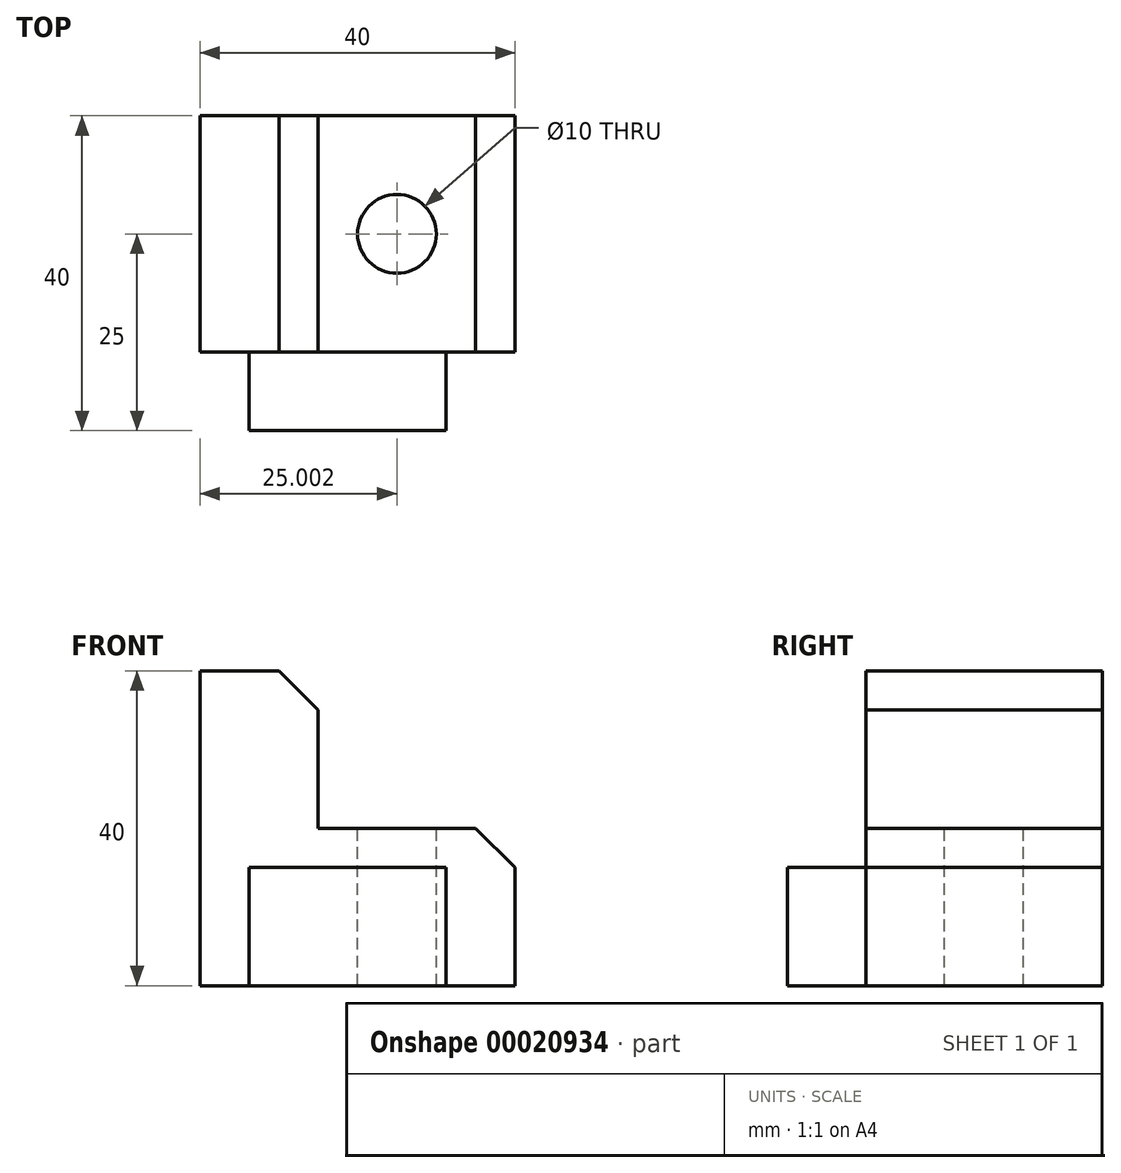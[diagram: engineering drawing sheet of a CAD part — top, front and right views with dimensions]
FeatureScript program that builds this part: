
annotation { "Feature Type Name" : "Feature", "Feature Type Description" : "" }
export const myFeature = defineFeature(function(context is Context, id is Id, definition is map)
    precondition{}
    {
        {
            var Q0;
            Q0=qCreatedBy(makeId("Front.planeOp"),FACE);
            var sketch = newSketch(context, id + "F0", { "sketchPlane" : qUnion([Q0])});
            skLineSegment(sketch, "E0", {"start": v(-37.6, 38.9) * mm, "end": v(-37.6, -1.1) * mm});
            skLineSegment(sketch, "E1", {"start": v(-37.6, -1.1) * mm, "end": v(2.4, -1.1) * mm});
            skLineSegment(sketch, "E2", {"start": v(2.4, -1.1) * mm, "end": v(2.4, 18.9) * mm});
            skLineSegment(sketch, "E3", {"start": v(2.4, 18.9) * mm, "end": v(-22.6, 18.9) * mm});
            skLineSegment(sketch, "E4", {"start": v(-22.6, 18.9) * mm, "end": v(-22.6, 38.9) * mm});
            skLineSegment(sketch, "E5", {"start": v(-22.6, 38.9) * mm, "end": v(-37.6, 38.9) * mm});
            skSolve(sketch);
        }
        {
            var Q0;
            Q0=makeQuery(id+"F0.imprint","IMPRINT",FACE,{"disambiguationData":[TD([[makeQuery(id+"F0.imprint","IMPRINT",EDGE,{"derivedFrom":sQuery(id+"F0.wireOp",EDGE,"E0")}),1.0]])]});
            extrude(context, id + "F1", {"entities" : qUnion([Q0]), "depth" : 30 * mm});
        }
        {
            var Q0;
            Q0=makeQuery(id+"F1.opExtrude","SWEPT_EDGE",EDGE,{"disambiguationData":[OSD([sQuery(id+"F0.wireOp",EDGE,"E4"),sQuery(id+"F0.wireOp",EDGE,"E5")])]});
            var Q1;
            Q1=makeQuery(id+"F1.opExtrude","SWEPT_EDGE",EDGE,{"disambiguationData":[OSD([sQuery(id+"F0.wireOp",EDGE,"E2"),sQuery(id+"F0.wireOp",EDGE,"E3")])]});
            chamfer(context, id + "F2", {"entities" : qUnion([Q0, Q1]), "width" : 5 * mm, "tangentPropagation" : true});
        }
        {
            var Q0;
            Q0=makeQuery(id+"F1.opExtrude","SWEPT_FACE",FACE,{"disambiguationData":[OSD([sQuery(id+"F0.wireOp",EDGE,"E3")])]});
            var sketch = newSketch(context, id + "F3", { "sketchPlane" : qUnion([Q0])});
            skCircle(sketch, "E6", {"center": v(-12.6, -15) * mm, "radius": 5 * mm});
            skSolve(sketch);
        }
        {
            var Q0;
            Q0=makeQuery(id+"F3.imprint","IMPRINT",FACE,{"disambiguationData":[TD([[makeQuery(id+"F3.imprint","IMPRINT",EDGE,{"derivedFrom":sQuery(id+"F3.wireOp",EDGE,"E6")}),1.0]])]});
            extrude(context, id + "F4", {"entities" : qUnion([Q0]), "operationType" : NewBodyOperationType.REMOVE, "endBound" : BoundingType.THROUGH_ALL, "oppositeDirection" : true, "depth" : 25 * mm});
        }
        {
            var Q0;
            Q0=makeQuery(id+"F1.opExtrude","CAP_FACE",FACE,{"disambiguationData":[OSD([sQuery(id+"F0.wireOp",EDGE,"E0"),sQuery(id+"F0.wireOp",EDGE,"E1"),sQuery(id+"F0.wireOp",EDGE,"E2"),sQuery(id+"F0.wireOp",EDGE,"E3"),sQuery(id+"F0.wireOp",EDGE,"E4"),sQuery(id+"F0.wireOp",EDGE,"E5")])],"isStart":false});
            var sketch = newSketch(context, id + "F5", { "sketchPlane" : qUnion([Q0])});
            skLineSegment(sketch, "E7.bottom", {"start": v(-31.38, -1.1) * mm, "end": v(-6.38, -1.1) * mm});
            skLineSegment(sketch, "E7.top", {"start": v(-31.38, 13.9) * mm, "end": v(-6.38, 13.9) * mm});
            skLineSegment(sketch, "E7.left", {"start": v(-31.38, -1.1) * mm, "end": v(-31.38, 13.9) * mm});
            skLineSegment(sketch, "E7.right", {"start": v(-6.38, -1.1) * mm, "end": v(-6.38, 13.9) * mm});
            skSolve(sketch);
        }
        {
            var Q0;
            Q0=makeQuery(id+"F5.imprint","IMPRINT",FACE,{"disambiguationData":[TD([[makeQuery(id+"F5.imprint","IMPRINT",EDGE,{"derivedFrom":sQuery(id+"F5.wireOp",EDGE,"E7.bottom")}),1.0]])]});
            extrude(context, id + "F6", {"entities" : qUnion([Q0]), "operationType" : NewBodyOperationType.ADD, "depth" : 10 * mm});
        }
    });
